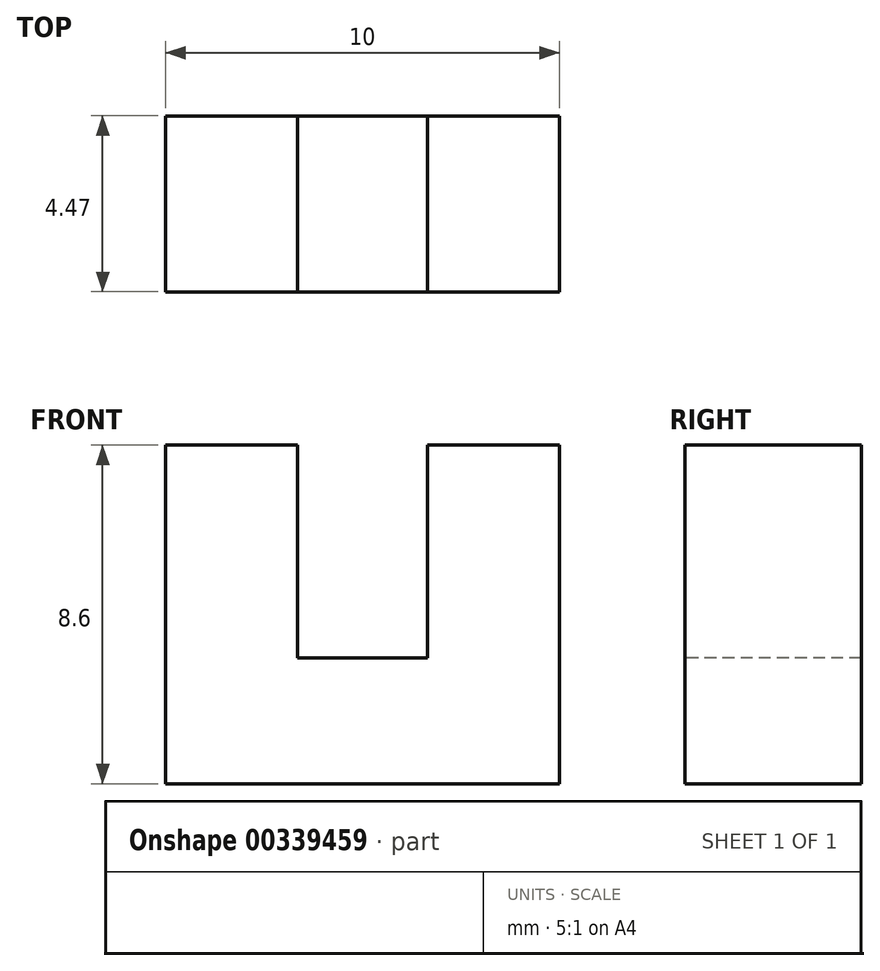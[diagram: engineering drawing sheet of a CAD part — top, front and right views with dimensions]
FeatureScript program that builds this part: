
annotation { "Feature Type Name" : "Feature", "Feature Type Description" : "" }
export const myFeature = defineFeature(function(context is Context, id is Id, definition is map)
    precondition{}
    {
        {
            var Q0;
            Q0=qCreatedBy(makeId("Top.planeOp"),FACE);
            var sketch = newSketch(context, id + "F0", { "sketchPlane" : qUnion([Q0])});
            skLineSegment(sketch, "E0.bottom", {"start": v(-10, -0.74) * mm, "end": v(0, -0.74) * mm});
            skLineSegment(sketch, "E0.top", {"start": v(-10, -5.21) * mm, "end": v(0, -5.21) * mm});
            skLineSegment(sketch, "E0.left", {"start": v(-10, -0.74) * mm, "end": v(-10, -5.21) * mm});
            skLineSegment(sketch, "E0.right", {"start": v(0, -0.74) * mm, "end": v(0, -5.21) * mm});
            skSolve(sketch);
        }
        {
            var Q0;
            Q0=qSketchRegion(id+"F0",true);
            extrude(context, id + "F1", {"entities" : qUnion([Q0]), "depth" : 3.2 * mm});
        }
        {
            var Q0;
            Q0=makeQuery(id+"F1.opExtrude","CAP_FACE",FACE,{"disambiguationData":[OSD([sQuery(id+"F0.wireOp",EDGE,"E0.bottom"),sQuery(id+"F0.wireOp",EDGE,"E0.top"),sQuery(id+"F0.wireOp",EDGE,"E0.left"),sQuery(id+"F0.wireOp",EDGE,"E0.right")])],"isStart":false});
            var sketch = newSketch(context, id + "F2", { "sketchPlane" : qUnion([Q0])});
            skLineSegment(sketch, "E1.bottom", {"start": v(-10, -0.74) * mm, "end": v(-6.65, -0.74) * mm});
            skLineSegment(sketch, "E1.top", {"start": v(-10, -5.21) * mm, "end": v(-6.65, -5.21) * mm});
            skLineSegment(sketch, "E1.left", {"start": v(-10, -0.74) * mm, "end": v(-10, -5.21) * mm});
            skLineSegment(sketch, "E1.right", {"start": v(-6.65, -0.74) * mm, "end": v(-6.65, -5.21) * mm});
            skLineSegment(sketch, "E2.bottom", {"start": v(0, -0.74) * mm, "end": v(-3.35, -0.74) * mm});
            skLineSegment(sketch, "E2.top", {"start": v(0, -5.21) * mm, "end": v(-3.35, -5.21) * mm});
            skLineSegment(sketch, "E2.left", {"start": v(0, -0.74) * mm, "end": v(0, -5.21) * mm});
            skLineSegment(sketch, "E2.right", {"start": v(-3.35, -0.74) * mm, "end": v(-3.35, -5.21) * mm});
            skSolve(sketch);
        }
        {
            var Q0;
            Q0=qSketchRegion(id+"F2",true);
            extrude(context, id + "F3", {"entities" : qUnion([Q0]), "operationType" : NewBodyOperationType.ADD, "depth" : 5.4 * mm});
        }
    });
